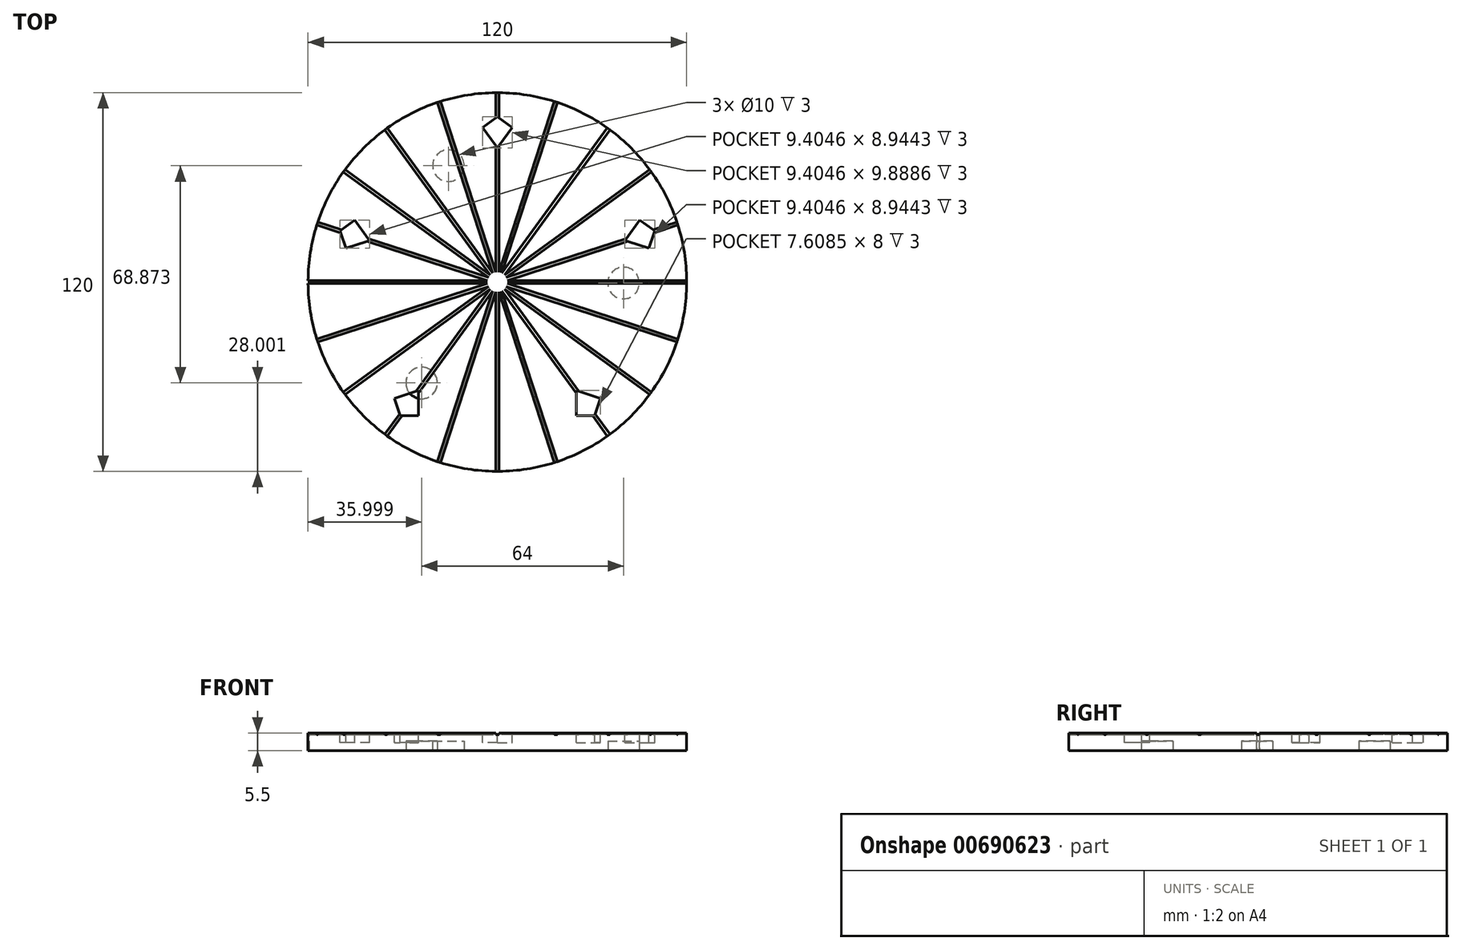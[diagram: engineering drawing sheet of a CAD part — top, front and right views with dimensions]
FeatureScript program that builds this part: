
annotation { "Feature Type Name" : "Feature", "Feature Type Description" : "" }
export const myFeature = defineFeature(function(context is Context, id is Id, definition is map)
    precondition{}
    {
        {
            var Q0;
            Q0=qCreatedBy(makeId("Top.planeOp"),FACE);
            var sketch = newSketch(context, id + "F0", { "sketchPlane" : qUnion([Q0])});
            skCircle(sketch, "E0", {"center": v(0, 0) * mm, "radius": 60 * mm});
            skSolve(sketch);
        }
        {
            var Q0;
            Q0=makeQuery(id+"F0.imprint","IMPRINT",FACE,{"disambiguationData":[TD([[makeQuery(id+"F0.imprint","IMPRINT",EDGE,{"derivedFrom":sQuery(id+"F0.wireOp",EDGE,"E0")}),1.0]])]});
            extrude(context, id + "F1", {"entities" : qUnion([Q0]), "depth" : 5 * mm, "offsetDistance" : 25 * mm});
        }
        {
            var Q0;
            Q0=makeQuery(id+"F1.opExtrude","CAP_FACE",FACE,{"disambiguationData":[OSD([sQuery(id+"F0.wireOp",EDGE,"E0")])],"isStart":false});
            var sketch = newSketch(context, id + "F2", { "sketchPlane" : qUnion([Q0])});
            skLineSegment(sketch, "E1.bottom", {"start": v(-100, 0.5) * mm, "end": v(0, 0.5) * mm});
            skLineSegment(sketch, "E1.top", {"start": v(-100, -0.5) * mm, "end": v(0, -0.5) * mm});
            skLineSegment(sketch, "E1.left", {"start": v(-100, 0.5) * mm, "end": v(-100, -0.5) * mm});
            skLineSegment(sketch, "E1.right", {"start": v(0, 0.5) * mm, "end": v(0, -0.5) * mm});
            skLineSegment(sketch, "E2.1.0", {"start": v(-95.26, -30.43) * mm, "end": v(-0.15, 0.48) * mm});
            skLineSegment(sketch, "E2.1.1", {"start": v(-94.95, -31.38) * mm, "end": v(0.15, -0.48) * mm});
            skLineSegment(sketch, "E2.1.2", {"start": v(-0.15, 0.48) * mm, "end": v(0.15, -0.48) * mm});
            skLineSegment(sketch, "E2.1.3", {"start": v(-95.26, -30.43) * mm, "end": v(-94.95, -31.38) * mm});
            skLineSegment(sketch, "E2.2.0", {"start": v(-81.2, -58.37) * mm, "end": v(-0.3, 0.4) * mm});
            skLineSegment(sketch, "E2.2.1", {"start": v(-80.6, -59.18) * mm, "end": v(0.3, -0.4) * mm});
            skLineSegment(sketch, "E2.2.2", {"start": v(-0.3, 0.4) * mm, "end": v(0.3, -0.4) * mm});
            skLineSegment(sketch, "E2.2.3", {"start": v(-81.2, -58.37) * mm, "end": v(-80.6, -59.18) * mm});
            skLineSegment(sketch, "E2.3.0", {"start": v(-59.18, -80.6) * mm, "end": v(-0.4, 0.3) * mm});
            skLineSegment(sketch, "E2.3.1", {"start": v(-58.37, -81.2) * mm, "end": v(0.4, -0.3) * mm});
            skLineSegment(sketch, "E2.3.2", {"start": v(-0.4, 0.3) * mm, "end": v(0.4, -0.3) * mm});
            skLineSegment(sketch, "E2.3.3", {"start": v(-59.18, -80.6) * mm, "end": v(-58.37, -81.2) * mm});
            skLineSegment(sketch, "E2.4.0", {"start": v(-31.38, -94.95) * mm, "end": v(-0.48, 0.15) * mm});
            skLineSegment(sketch, "E2.4.1", {"start": v(-30.43, -95.26) * mm, "end": v(0.48, -0.15) * mm});
            skLineSegment(sketch, "E2.4.2", {"start": v(-0.48, 0.15) * mm, "end": v(0.48, -0.15) * mm});
            skLineSegment(sketch, "E2.4.3", {"start": v(-31.38, -94.95) * mm, "end": v(-30.43, -95.26) * mm});
            skLineSegment(sketch, "E2.5.0", {"start": v(-0.5, -100) * mm, "end": v(-0.5, 0) * mm});
            skLineSegment(sketch, "E2.5.1", {"start": v(0.5, -100) * mm, "end": v(0.5, 0) * mm});
            skLineSegment(sketch, "E2.5.2", {"start": v(-0.5, 0) * mm, "end": v(0.5, 0) * mm});
            skLineSegment(sketch, "E2.5.3", {"start": v(-0.5, -100) * mm, "end": v(0.5, -100) * mm});
            skLineSegment(sketch, "E2.6.0", {"start": v(30.43, -95.26) * mm, "end": v(-0.48, -0.15) * mm});
            skLineSegment(sketch, "E2.6.1", {"start": v(31.38, -94.95) * mm, "end": v(0.48, 0.15) * mm});
            skLineSegment(sketch, "E2.6.2", {"start": v(-0.48, -0.15) * mm, "end": v(0.48, 0.15) * mm});
            skLineSegment(sketch, "E2.6.3", {"start": v(30.43, -95.26) * mm, "end": v(31.38, -94.95) * mm});
            skLineSegment(sketch, "E2.7.0", {"start": v(58.37, -81.2) * mm, "end": v(-0.4, -0.3) * mm});
            skLineSegment(sketch, "E2.7.1", {"start": v(59.18, -80.6) * mm, "end": v(0.4, 0.3) * mm});
            skLineSegment(sketch, "E2.7.2", {"start": v(-0.4, -0.3) * mm, "end": v(0.4, 0.3) * mm});
            skLineSegment(sketch, "E2.7.3", {"start": v(58.37, -81.2) * mm, "end": v(59.18, -80.6) * mm});
            skLineSegment(sketch, "E2.8.0", {"start": v(80.6, -59.18) * mm, "end": v(-0.3, -0.4) * mm});
            skLineSegment(sketch, "E2.8.1", {"start": v(81.2, -58.37) * mm, "end": v(0.3, 0.4) * mm});
            skLineSegment(sketch, "E2.8.2", {"start": v(-0.3, -0.4) * mm, "end": v(0.3, 0.4) * mm});
            skLineSegment(sketch, "E2.8.3", {"start": v(80.6, -59.18) * mm, "end": v(81.2, -58.37) * mm});
            skLineSegment(sketch, "E2.9.0", {"start": v(94.95, -31.38) * mm, "end": v(-0.15, -0.48) * mm});
            skLineSegment(sketch, "E2.9.1", {"start": v(95.26, -30.43) * mm, "end": v(0.15, 0.48) * mm});
            skLineSegment(sketch, "E2.9.2", {"start": v(-0.15, -0.48) * mm, "end": v(0.15, 0.48) * mm});
            skLineSegment(sketch, "E2.9.3", {"start": v(94.95, -31.38) * mm, "end": v(95.26, -30.43) * mm});
            skLineSegment(sketch, "E2.10.0", {"start": v(100, -0.5) * mm, "end": v(0, -0.5) * mm});
            skLineSegment(sketch, "E2.10.1", {"start": v(100, 0.5) * mm, "end": v(0, 0.5) * mm});
            skLineSegment(sketch, "E2.10.2", {"start": v(0, -0.5) * mm, "end": v(0, 0.5) * mm});
            skLineSegment(sketch, "E2.10.3", {"start": v(100, -0.5) * mm, "end": v(100, 0.5) * mm});
            skLineSegment(sketch, "E2.11.0", {"start": v(95.26, 30.43) * mm, "end": v(0.15, -0.48) * mm});
            skLineSegment(sketch, "E2.11.1", {"start": v(94.95, 31.38) * mm, "end": v(-0.15, 0.48) * mm});
            skLineSegment(sketch, "E2.11.2", {"start": v(0.15, -0.48) * mm, "end": v(-0.15, 0.48) * mm});
            skLineSegment(sketch, "E2.11.3", {"start": v(95.26, 30.43) * mm, "end": v(94.95, 31.38) * mm});
            skLineSegment(sketch, "E2.12.0", {"start": v(81.2, 58.37) * mm, "end": v(0.3, -0.4) * mm});
            skLineSegment(sketch, "E2.12.1", {"start": v(80.6, 59.18) * mm, "end": v(-0.3, 0.4) * mm});
            skLineSegment(sketch, "E2.12.2", {"start": v(0.3, -0.4) * mm, "end": v(-0.3, 0.4) * mm});
            skLineSegment(sketch, "E2.12.3", {"start": v(81.2, 58.37) * mm, "end": v(80.6, 59.18) * mm});
            skLineSegment(sketch, "E2.13.0", {"start": v(59.18, 80.6) * mm, "end": v(0.4, -0.3) * mm});
            skLineSegment(sketch, "E2.13.1", {"start": v(58.37, 81.2) * mm, "end": v(-0.4, 0.3) * mm});
            skLineSegment(sketch, "E2.13.2", {"start": v(0.4, -0.3) * mm, "end": v(-0.4, 0.3) * mm});
            skLineSegment(sketch, "E2.13.3", {"start": v(59.18, 80.6) * mm, "end": v(58.37, 81.2) * mm});
            skLineSegment(sketch, "E2.14.0", {"start": v(31.38, 94.95) * mm, "end": v(0.48, -0.15) * mm});
            skLineSegment(sketch, "E2.14.1", {"start": v(30.43, 95.26) * mm, "end": v(-0.48, 0.15) * mm});
            skLineSegment(sketch, "E2.14.2", {"start": v(0.48, -0.15) * mm, "end": v(-0.48, 0.15) * mm});
            skLineSegment(sketch, "E2.14.3", {"start": v(31.38, 94.95) * mm, "end": v(30.43, 95.26) * mm});
            skLineSegment(sketch, "E2.15.0", {"start": v(0.5, 100) * mm, "end": v(0.5, 0) * mm});
            skLineSegment(sketch, "E2.15.1", {"start": v(-0.5, 100) * mm, "end": v(-0.5, 0) * mm});
            skLineSegment(sketch, "E2.15.2", {"start": v(0.5, 0) * mm, "end": v(-0.5, 0) * mm});
            skLineSegment(sketch, "E2.15.3", {"start": v(0.5, 100) * mm, "end": v(-0.5, 100) * mm});
            skLineSegment(sketch, "E2.16.0", {"start": v(-30.43, 95.26) * mm, "end": v(0.48, 0.15) * mm});
            skLineSegment(sketch, "E2.16.1", {"start": v(-31.38, 94.95) * mm, "end": v(-0.48, -0.15) * mm});
            skLineSegment(sketch, "E2.16.2", {"start": v(0.48, 0.15) * mm, "end": v(-0.48, -0.15) * mm});
            skLineSegment(sketch, "E2.16.3", {"start": v(-30.43, 95.26) * mm, "end": v(-31.38, 94.95) * mm});
            skLineSegment(sketch, "E2.17.0", {"start": v(-58.37, 81.2) * mm, "end": v(0.4, 0.3) * mm});
            skLineSegment(sketch, "E2.17.1", {"start": v(-59.18, 80.6) * mm, "end": v(-0.4, -0.3) * mm});
            skLineSegment(sketch, "E2.17.2", {"start": v(0.4, 0.3) * mm, "end": v(-0.4, -0.3) * mm});
            skLineSegment(sketch, "E2.17.3", {"start": v(-58.37, 81.2) * mm, "end": v(-59.18, 80.6) * mm});
            skLineSegment(sketch, "E2.18.0", {"start": v(-80.6, 59.18) * mm, "end": v(0.3, 0.4) * mm});
            skLineSegment(sketch, "E2.18.1", {"start": v(-81.2, 58.37) * mm, "end": v(-0.3, -0.4) * mm});
            skLineSegment(sketch, "E2.18.2", {"start": v(0.3, 0.4) * mm, "end": v(-0.3, -0.4) * mm});
            skLineSegment(sketch, "E2.18.3", {"start": v(-80.6, 59.18) * mm, "end": v(-81.2, 58.37) * mm});
            skLineSegment(sketch, "E2.19.0", {"start": v(-94.95, 31.38) * mm, "end": v(0.15, 0.48) * mm});
            skLineSegment(sketch, "E2.19.1", {"start": v(-95.26, 30.43) * mm, "end": v(-0.15, -0.48) * mm});
            skLineSegment(sketch, "E2.19.2", {"start": v(0.15, 0.48) * mm, "end": v(-0.15, -0.48) * mm});
            skLineSegment(sketch, "E2.19.3", {"start": v(-94.95, 31.38) * mm, "end": v(-95.26, 30.43) * mm});
            skPoint(sketch, "E2.center", {"position": v(0, 0) * mm});
            skSolve(sketch);
        }
        {
            var Q0;
            {var subQ0=sQuery(id+"F2.wireOp",EDGE,"E2.11.0");var subQ1=sQuery(id+"F2.wireOp",EDGE,"E2.10.1");var subQ2=makeQuery(id+"F2.imprint","INTERSECT",VERTEX,{"derivedFrom":[subQ1,subQ0]});Q0=makeQuery(id+"F2.imprint","IMPRINT",FACE,{"disambiguationData":[TD([[makeQuery(id+"F2.imprint","IMPRINT",EDGE,{"disambiguationData":[TD([[subQ2,1.0]])],"derivedFrom":subQ1}),-1.0]])]});}
            var Q1;
            {var subQ0=sQuery(id+"F2.wireOp",EDGE,"E2.12.0");var subQ1=sQuery(id+"F2.wireOp",EDGE,"E2.11.1");var subQ2=makeQuery(id+"F2.imprint","INTERSECT",VERTEX,{"derivedFrom":[subQ1,subQ0]});Q1=makeQuery(id+"F2.imprint","IMPRINT",FACE,{"disambiguationData":[TD([[makeQuery(id+"F2.imprint","IMPRINT",EDGE,{"disambiguationData":[TD([[subQ2,1.0]])],"derivedFrom":subQ1}),-1.0]])]});}
            var Q2;
            {var subQ0=sQuery(id+"F2.wireOp",EDGE,"E2.13.0");var subQ1=sQuery(id+"F2.wireOp",EDGE,"E2.12.1");var subQ2=makeQuery(id+"F2.imprint","INTERSECT",VERTEX,{"derivedFrom":[subQ1,subQ0]});Q2=makeQuery(id+"F2.imprint","IMPRINT",FACE,{"disambiguationData":[TD([[makeQuery(id+"F2.imprint","IMPRINT",EDGE,{"disambiguationData":[TD([[subQ2,1.0]])],"derivedFrom":subQ1}),-1.0]])]});}
            var Q3;
            {var subQ0=sQuery(id+"F2.wireOp",EDGE,"E2.14.0");var subQ1=sQuery(id+"F2.wireOp",EDGE,"E2.13.1");var subQ2=makeQuery(id+"F2.imprint","INTERSECT",VERTEX,{"derivedFrom":[subQ1,subQ0]});Q3=makeQuery(id+"F2.imprint","IMPRINT",FACE,{"disambiguationData":[TD([[makeQuery(id+"F2.imprint","IMPRINT",EDGE,{"disambiguationData":[TD([[subQ2,1.0]])],"derivedFrom":subQ1}),-1.0]])]});}
            var Q4;
            {var subQ0=sQuery(id+"F2.wireOp",EDGE,"E2.15.0");var subQ1=sQuery(id+"F2.wireOp",EDGE,"E2.14.1");var subQ2=makeQuery(id+"F2.imprint","INTERSECT",VERTEX,{"derivedFrom":[subQ1,subQ0]});Q4=makeQuery(id+"F2.imprint","IMPRINT",FACE,{"disambiguationData":[TD([[makeQuery(id+"F2.imprint","IMPRINT",EDGE,{"disambiguationData":[TD([[subQ2,1.0]])],"derivedFrom":subQ1}),-1.0]])]});}
            var Q5;
            {var subQ0=sQuery(id+"F2.wireOp",EDGE,"E2.16.0");var subQ1=sQuery(id+"F2.wireOp",EDGE,"E2.15.1");var subQ2=makeQuery(id+"F2.imprint","INTERSECT",VERTEX,{"derivedFrom":[subQ1,subQ0]});Q5=makeQuery(id+"F2.imprint","IMPRINT",FACE,{"disambiguationData":[TD([[makeQuery(id+"F2.imprint","IMPRINT",EDGE,{"disambiguationData":[TD([[subQ2,1.0]])],"derivedFrom":subQ1}),-1.0]])]});}
            var Q6;
            {var subQ0=sQuery(id+"F2.wireOp",EDGE,"E2.17.0");var subQ1=sQuery(id+"F2.wireOp",EDGE,"E2.16.1");var subQ2=makeQuery(id+"F2.imprint","INTERSECT",VERTEX,{"derivedFrom":[subQ1,subQ0]});Q6=makeQuery(id+"F2.imprint","IMPRINT",FACE,{"disambiguationData":[TD([[makeQuery(id+"F2.imprint","IMPRINT",EDGE,{"disambiguationData":[TD([[subQ2,1.0]])],"derivedFrom":subQ1}),-1.0]])]});}
            var Q7;
            {var subQ0=sQuery(id+"F2.wireOp",EDGE,"E2.18.0");var subQ1=sQuery(id+"F2.wireOp",EDGE,"E2.17.1");var subQ2=makeQuery(id+"F2.imprint","INTERSECT",VERTEX,{"derivedFrom":[subQ1,subQ0]});Q7=makeQuery(id+"F2.imprint","IMPRINT",FACE,{"disambiguationData":[TD([[makeQuery(id+"F2.imprint","IMPRINT",EDGE,{"disambiguationData":[TD([[subQ2,1.0]])],"derivedFrom":subQ1}),-1.0]])]});}
            var Q8;
            {var subQ0=sQuery(id+"F2.wireOp",EDGE,"E2.19.0");var subQ1=sQuery(id+"F2.wireOp",EDGE,"E2.18.1");var subQ2=makeQuery(id+"F2.imprint","INTERSECT",VERTEX,{"derivedFrom":[subQ1,subQ0]});Q8=makeQuery(id+"F2.imprint","IMPRINT",FACE,{"disambiguationData":[TD([[makeQuery(id+"F2.imprint","IMPRINT",EDGE,{"disambiguationData":[TD([[subQ2,1.0]])],"derivedFrom":subQ1}),-1.0]])]});}
            var Q9;
            {var subQ0=sQuery(id+"F2.wireOp",EDGE,"E2.19.1");var subQ1=sQuery(id+"F2.wireOp",EDGE,"E1.bottom");var subQ2=makeQuery(id+"F2.imprint","INTERSECT",VERTEX,{"derivedFrom":[subQ1,subQ0]});Q9=makeQuery(id+"F2.imprint","IMPRINT",FACE,{"disambiguationData":[TD([[makeQuery(id+"F2.imprint","IMPRINT",EDGE,{"disambiguationData":[TD([[subQ2,1.0]])],"derivedFrom":subQ1}),1.0]])]});}
            var Q10;
            {var subQ0=sQuery(id+"F2.wireOp",EDGE,"E2.1.0");var subQ1=sQuery(id+"F2.wireOp",EDGE,"E1.top");var subQ2=makeQuery(id+"F2.imprint","INTERSECT",VERTEX,{"derivedFrom":[subQ1,subQ0]});Q10=makeQuery(id+"F2.imprint","IMPRINT",FACE,{"disambiguationData":[TD([[makeQuery(id+"F2.imprint","IMPRINT",EDGE,{"disambiguationData":[TD([[subQ2,1.0]])],"derivedFrom":subQ1}),-1.0]])]});}
            var Q11;
            {var subQ0=sQuery(id+"F2.wireOp",EDGE,"E2.2.0");var subQ1=sQuery(id+"F2.wireOp",EDGE,"E2.1.1");var subQ2=makeQuery(id+"F2.imprint","INTERSECT",VERTEX,{"derivedFrom":[subQ1,subQ0]});Q11=makeQuery(id+"F2.imprint","IMPRINT",FACE,{"disambiguationData":[TD([[makeQuery(id+"F2.imprint","IMPRINT",EDGE,{"disambiguationData":[TD([[subQ2,1.0]])],"derivedFrom":subQ1}),-1.0]])]});}
            var Q12;
            {var subQ0=sQuery(id+"F2.wireOp",EDGE,"E2.3.0");var subQ1=sQuery(id+"F2.wireOp",EDGE,"E2.2.1");var subQ2=makeQuery(id+"F2.imprint","INTERSECT",VERTEX,{"derivedFrom":[subQ1,subQ0]});Q12=makeQuery(id+"F2.imprint","IMPRINT",FACE,{"disambiguationData":[TD([[makeQuery(id+"F2.imprint","IMPRINT",EDGE,{"disambiguationData":[TD([[subQ2,1.0]])],"derivedFrom":subQ1}),-1.0]])]});}
            var Q13;
            {var subQ0=sQuery(id+"F2.wireOp",EDGE,"E2.4.0");var subQ1=sQuery(id+"F2.wireOp",EDGE,"E2.3.1");var subQ2=makeQuery(id+"F2.imprint","INTERSECT",VERTEX,{"derivedFrom":[subQ1,subQ0]});Q13=makeQuery(id+"F2.imprint","IMPRINT",FACE,{"disambiguationData":[TD([[makeQuery(id+"F2.imprint","IMPRINT",EDGE,{"disambiguationData":[TD([[subQ2,1.0]])],"derivedFrom":subQ1}),-1.0]])]});}
            var Q14;
            {var subQ0=sQuery(id+"F2.wireOp",EDGE,"E2.5.0");var subQ1=sQuery(id+"F2.wireOp",EDGE,"E2.4.1");var subQ2=makeQuery(id+"F2.imprint","INTERSECT",VERTEX,{"derivedFrom":[subQ1,subQ0]});Q14=makeQuery(id+"F2.imprint","IMPRINT",FACE,{"disambiguationData":[TD([[makeQuery(id+"F2.imprint","IMPRINT",EDGE,{"disambiguationData":[TD([[subQ2,1.0]])],"derivedFrom":subQ1}),-1.0]])]});}
            var Q15;
            {var subQ0=sQuery(id+"F2.wireOp",EDGE,"E2.6.0");var subQ1=sQuery(id+"F2.wireOp",EDGE,"E2.5.1");var subQ2=makeQuery(id+"F2.imprint","INTERSECT",VERTEX,{"derivedFrom":[subQ1,subQ0]});Q15=makeQuery(id+"F2.imprint","IMPRINT",FACE,{"disambiguationData":[TD([[makeQuery(id+"F2.imprint","IMPRINT",EDGE,{"disambiguationData":[TD([[subQ2,1.0]])],"derivedFrom":subQ1}),-1.0]])]});}
            var Q16;
            {var subQ0=sQuery(id+"F2.wireOp",EDGE,"E2.7.0");var subQ1=sQuery(id+"F2.wireOp",EDGE,"E2.6.1");var subQ2=makeQuery(id+"F2.imprint","INTERSECT",VERTEX,{"derivedFrom":[subQ1,subQ0]});Q16=makeQuery(id+"F2.imprint","IMPRINT",FACE,{"disambiguationData":[TD([[makeQuery(id+"F2.imprint","IMPRINT",EDGE,{"disambiguationData":[TD([[subQ2,1.0]])],"derivedFrom":subQ1}),-1.0]])]});}
            var Q17;
            {var subQ0=sQuery(id+"F2.wireOp",EDGE,"E2.8.0");var subQ1=sQuery(id+"F2.wireOp",EDGE,"E2.7.1");var subQ2=makeQuery(id+"F2.imprint","INTERSECT",VERTEX,{"derivedFrom":[subQ1,subQ0]});Q17=makeQuery(id+"F2.imprint","IMPRINT",FACE,{"disambiguationData":[TD([[makeQuery(id+"F2.imprint","IMPRINT",EDGE,{"disambiguationData":[TD([[subQ2,1.0]])],"derivedFrom":subQ1}),-1.0]])]});}
            var Q18;
            {var subQ0=sQuery(id+"F2.wireOp",EDGE,"E2.9.0");var subQ1=sQuery(id+"F2.wireOp",EDGE,"E2.8.1");var subQ2=makeQuery(id+"F2.imprint","INTERSECT",VERTEX,{"derivedFrom":[subQ1,subQ0]});Q18=makeQuery(id+"F2.imprint","IMPRINT",FACE,{"disambiguationData":[TD([[makeQuery(id+"F2.imprint","IMPRINT",EDGE,{"disambiguationData":[TD([[subQ2,1.0]])],"derivedFrom":subQ1}),-1.0]])]});}
            var Q19;
            {var subQ0=sQuery(id+"F2.wireOp",EDGE,"E2.10.0");var subQ1=sQuery(id+"F2.wireOp",EDGE,"E2.9.1");var subQ2=makeQuery(id+"F2.imprint","INTERSECT",VERTEX,{"derivedFrom":[subQ1,subQ0]});Q19=makeQuery(id+"F2.imprint","IMPRINT",FACE,{"disambiguationData":[TD([[makeQuery(id+"F2.imprint","IMPRINT",EDGE,{"disambiguationData":[TD([[subQ2,1.0]])],"derivedFrom":subQ1}),-1.0]])]});}
            extrude(context, id + "F3", {"entities" : qUnion([Q0, Q1, Q2, Q3, Q4, Q5, Q6, Q7, Q8, Q9, Q10, Q11, Q12, Q13, Q14, Q15, Q16, Q17, Q18, Q19]), "operationType" : NewBodyOperationType.ADD, "depth" : 0.5 * mm, "offsetDistance" : 25 * mm});
        }
        {
            var Q0;
            Q0=makeQuery(id+"F3.opExtrude","CAP_FACE",FACE,{"disambiguationData":[OSD([sQuery(id+"F0.wireOp",EDGE,"E0"),sQuery(id+"F2.wireOp",EDGE,"E1.top"),sQuery(id+"F2.wireOp",EDGE,"E2.1.0")])],"isStart":false});
            var sketch = newSketch(context, id + "F4", { "sketchPlane" : qUnion([Q0])});
            skLineSegment(sketch, "E3.bottom", {"start": v(-64.5, 0.5) * mm, "end": v(-59.5, 0.5) * mm});
            skLineSegment(sketch, "E3.top", {"start": v(-64.5, -0.5) * mm, "end": v(-59.5, -0.5) * mm});
            skLineSegment(sketch, "E3.left", {"start": v(-64.5, 0.5) * mm, "end": v(-64.5, -0.5) * mm});
            skLineSegment(sketch, "E3.right", {"start": v(-59.5, 0.5) * mm, "end": v(-59.5, -0.5) * mm});
            skSolve(sketch);
        }
        {
            var Q0;
            Q0 = qSketchRegion(id + "F4", true);
            extrude(context, id + "F5", {"entities" : qUnion([Q0]), "operationType" : NewBodyOperationType.REMOVE, "endBound" : BoundingType.THROUGH_ALL, "oppositeDirection" : true, "depth" : 25 * mm, "offsetDistance" : 25 * mm});
        }
        {
            var Q0;
            Q0=qCreatedBy(makeId("Front.planeOp"),FACE);
            var sketch = newSketch(context, id + "F6", { "sketchPlane" : qUnion([Q0])});
            skLineSegment(sketch, "E4", {"start": v(0, 0) * mm, "end": v(0, 68.97) * mm, "construction": true});
            skSolve(sketch);
        }
        {
            var Q0;
            Q0=makeQuery(id+"F3.opExtrude","CAP_FACE",FACE,{"disambiguationData":[OSD([sQuery(id+"F0.wireOp",EDGE,"E0"),sQuery(id+"F2.wireOp",EDGE,"E2.18.1"),sQuery(id+"F2.wireOp",EDGE,"E2.19.0")])],"isStart":false});
            var sketch = newSketch(context, id + "F7", { "sketchPlane" : qUnion([Q0])});
            skCircle(sketch, "E5.cCircle", {"center": v(0, 0) * mm, "radius": 34.4 * mm, "construction": true});
            skLineSegment(sketch, "E5.0", {"start": v(25, -34.4) * mm, "end": v(-25, -34.4) * mm});
            skLineSegment(sketch, "E5.1", {"start": v(-25, -34.4) * mm, "end": v(-40.45, 13.14) * mm});
            skLineSegment(sketch, "E5.2", {"start": v(-40.45, 13.14) * mm, "end": v(0, 42.53) * mm});
            skLineSegment(sketch, "E5.3", {"start": v(0, 42.53) * mm, "end": v(40.45, 13.14) * mm});
            skLineSegment(sketch, "E5.4", {"start": v(40.45, 13.14) * mm, "end": v(25, -34.4) * mm});
            skPoint(sketch, "E5.0.midPoint", {"position": v(0, -34.4) * mm});
            skLineSegment(sketch, "E6.0", {"start": v(48.06, 10.67) * mm, "end": v(32.6, -36.88) * mm});
            skLineSegment(sketch, "E7.0", {"start": v(25, -42.4) * mm, "end": v(-25, -42.4) * mm});
            skLineSegment(sketch, "E8", {"start": v(25, -34.4) * mm, "end": v(25, -42.4) * mm});
            skLineSegment(sketch, "E9", {"start": v(25, -34.4) * mm, "end": v(32.6, -36.88) * mm});
            skLineSegment(sketch, "E10", {"start": v(25, -42.4) * mm, "end": v(30.81, -42.4) * mm});
            skLineSegment(sketch, "E11", {"start": v(32.6, -36.88) * mm, "end": v(30.81, -42.4) * mm});
            skLineSegment(sketch, "E12.1.0", {"start": v(40.45, 13.14) * mm, "end": v(48.06, 10.67) * mm});
            skLineSegment(sketch, "E12.1.1", {"start": v(48.06, 10.67) * mm, "end": v(49.86, 16.2) * mm});
            skLineSegment(sketch, "E12.1.2", {"start": v(45.15, 19.62) * mm, "end": v(49.86, 16.2) * mm});
            skLineSegment(sketch, "E12.1.3", {"start": v(40.45, 13.14) * mm, "end": v(45.15, 19.62) * mm});
            skLineSegment(sketch, "E12.2.0", {"start": v(0, 42.53) * mm, "end": v(4.7, 49) * mm});
            skLineSegment(sketch, "E12.2.1", {"start": v(4.7, 49) * mm, "end": v(0, 52.42) * mm});
            skLineSegment(sketch, "E12.2.2", {"start": v(-4.7, 49) * mm, "end": v(0, 52.42) * mm});
            skLineSegment(sketch, "E12.2.3", {"start": v(0, 42.53) * mm, "end": v(-4.7, 49) * mm});
            skLineSegment(sketch, "E12.3.0", {"start": v(-40.45, 13.14) * mm, "end": v(-45.15, 19.62) * mm});
            skLineSegment(sketch, "E12.3.1", {"start": v(-45.15, 19.62) * mm, "end": v(-49.86, 16.2) * mm});
            skLineSegment(sketch, "E12.3.2", {"start": v(-48.06, 10.67) * mm, "end": v(-49.86, 16.2) * mm});
            skLineSegment(sketch, "E12.3.3", {"start": v(-40.45, 13.14) * mm, "end": v(-48.06, 10.67) * mm});
            skLineSegment(sketch, "E12.4.0", {"start": v(-25, -34.4) * mm, "end": v(-32.6, -36.88) * mm});
            skLineSegment(sketch, "E12.4.1", {"start": v(-32.6, -36.88) * mm, "end": v(-30.81, -42.4) * mm});
            skLineSegment(sketch, "E12.4.2", {"start": v(-25, -42.4) * mm, "end": v(-30.81, -42.4) * mm});
            skLineSegment(sketch, "E12.4.3", {"start": v(-25, -34.4) * mm, "end": v(-25, -42.4) * mm});
            skSolve(sketch);
        }
        {
            var Q0;
            Q0=makeQuery(id+"F7.imprint","IMPRINT",FACE,{"disambiguationData":[TD([[makeQuery(id+"F7.imprint","IMPRINT",EDGE,{"derivedFrom":sQuery(id+"F7.wireOp",EDGE,"E12.2.0")}),1.0]])]});
            var Q1;
            {var subQ0=sQuery(id+"F7.wireOp",EDGE,"E12.3.2");Q1=makeQuery(id+"F7.imprint","IMPRINT",FACE,{"disambiguationData":[TD([[makeQuery(id+"F7.imprint","IMPRINT",EDGE,{"derivedFrom":subQ0}),-1.0]])]});}
            var Q2;
            {var subQ0=sQuery(id+"F7.wireOp",EDGE,"E12.3.1");var subQ1=sQuery(id+"F7.wireOp",EDGE,"E12.3.0");var subQ2=makeQuery(id+"F7.imprint","INTERSECT",VERTEX,{"derivedFrom":[subQ1,subQ0]});Q2=makeQuery(id+"F7.imprint","IMPRINT",FACE,{"disambiguationData":[TD([[makeQuery(id+"F7.imprint","IMPRINT",EDGE,{"disambiguationData":[TD([[subQ2,1.0]])],"derivedFrom":subQ1}),1.0]])]});}
            var Q3;
            Q3=makeQuery(id+"F7.imprint","IMPRINT",FACE,{"disambiguationData":[TD([[makeQuery(id+"F7.imprint","IMPRINT",EDGE,{"derivedFrom":sQuery(id+"F7.wireOp",EDGE,"E12.1.0")}),1.0]])]});
            var Q4;
            Q4=makeQuery(id+"F7.imprint","IMPRINT",FACE,{"disambiguationData":[TD([[makeQuery(id+"F7.imprint","IMPRINT",EDGE,{"derivedFrom":sQuery(id+"F7.wireOp",EDGE,"E12.4.0")}),1.0]])]});
            var Q5;
            Q5=makeQuery(id+"F7.imprint","IMPRINT",FACE,{"disambiguationData":[TD([[makeQuery(id+"F7.imprint","IMPRINT",EDGE,{"derivedFrom":sQuery(id+"F7.wireOp",EDGE,"E8")}),1.0]])]});
            extrude(context, id + "F8", {"entities" : qUnion([Q0, Q1, Q2, Q3, Q4, Q5]), "operationType" : NewBodyOperationType.REMOVE, "oppositeDirection" : true, "depth" : 3 * mm, "offsetDistance" : 25 * mm});
        }
        {
            var Q0;
            Q0=makeQuery(id+"F1.opExtrude","CAP_FACE",FACE,{"disambiguationData":[OSD([sQuery(id+"F0.wireOp",EDGE,"E0")])],"isStart":true});
            var sketch = newSketch(context, id + "F9", { "sketchPlane" : qUnion([Q0])});
            skCircle(sketch, "E13", {"center": v(0, 0) * mm, "radius": 40 * mm, "construction": true});
            skCircle(sketch, "E14", {"center": v(40, 0.31) * mm, "radius": 5 * mm});
            skCircle(sketch, "E15", {"center": v(-24, 32) * mm, "radius": 5 * mm});
            skCircle(sketch, "E16", {"center": v(-15.5, -36.87) * mm, "radius": 5 * mm});
            skSolve(sketch);
        }
        {
            var Q0;
            Q0=makeQuery(id+"F9.imprint","IMPRINT",FACE,{"disambiguationData":[TD([[makeQuery(id+"F9.imprint","IMPRINT",EDGE,{"derivedFrom":sQuery(id+"F9.wireOp",EDGE,"E15")}),1.0]])]});
            var Q1;
            Q1=makeQuery(id+"F9.imprint","IMPRINT",FACE,{"disambiguationData":[TD([[makeQuery(id+"F9.imprint","IMPRINT",EDGE,{"derivedFrom":sQuery(id+"F9.wireOp",EDGE,"E16")}),1.0]])]});
            var Q2;
            Q2=makeQuery(id+"F9.imprint","IMPRINT",FACE,{"disambiguationData":[TD([[makeQuery(id+"F9.imprint","IMPRINT",EDGE,{"derivedFrom":sQuery(id+"F9.wireOp",EDGE,"E14")}),1.0]])]});
            extrude(context, id + "F10", {"entities" : qUnion([Q0, Q1, Q2]), "operationType" : NewBodyOperationType.REMOVE, "oppositeDirection" : true, "depth" : 3 * mm, "offsetDistance" : 25 * mm});
        }
    });
